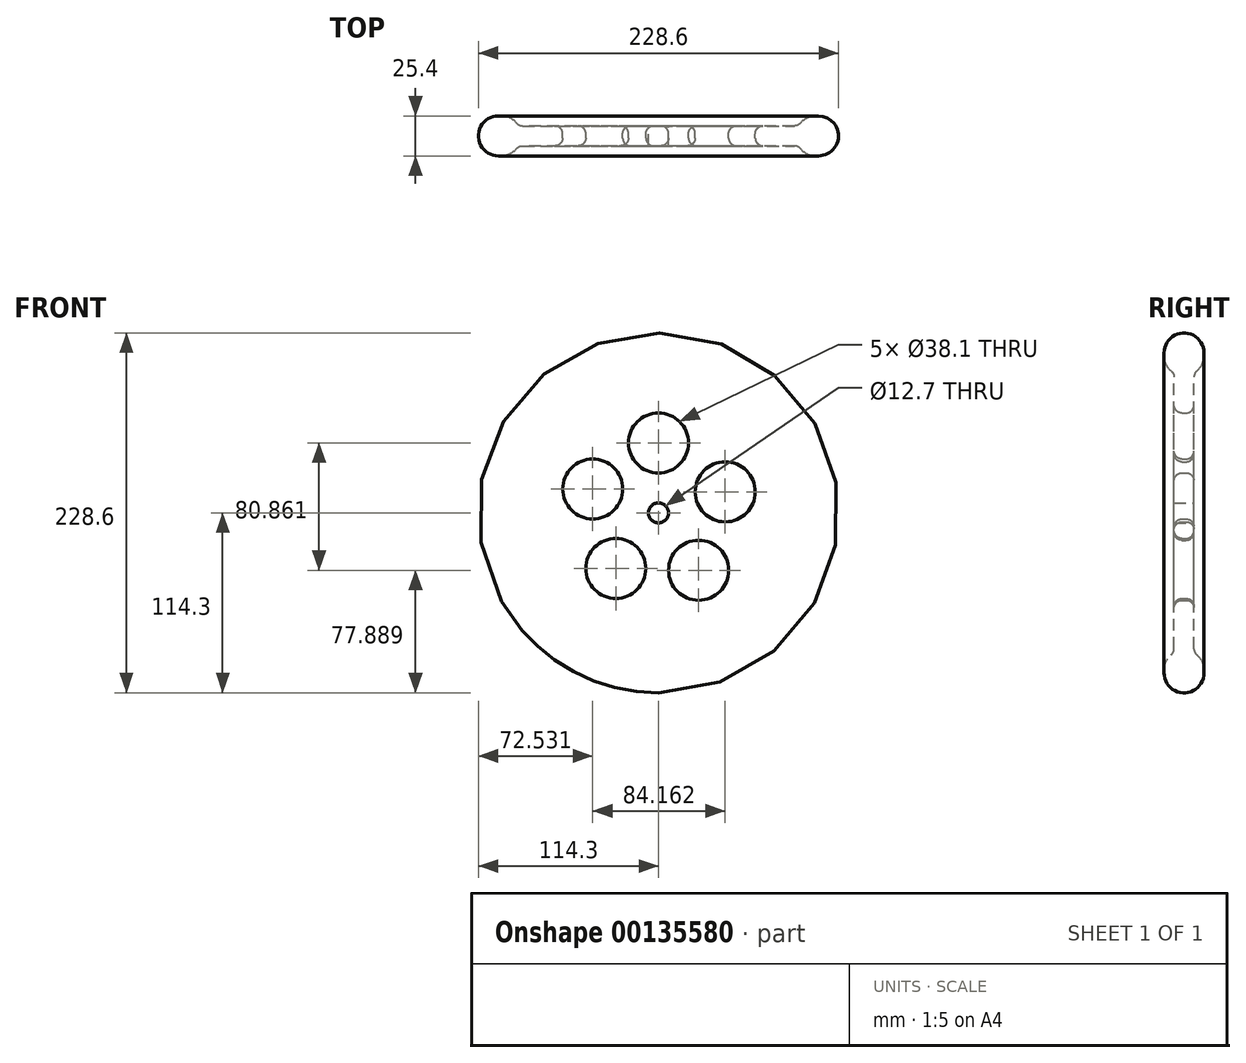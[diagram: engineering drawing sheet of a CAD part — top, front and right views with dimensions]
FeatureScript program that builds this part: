
annotation { "Feature Type Name" : "Feature", "Feature Type Description" : "" }
export const myFeature = defineFeature(function(context is Context, id is Id, definition is map)
    precondition{}
    {
        {
            var Q0;
            Q0=qCreatedBy(makeId("Front.planeOp"),FACE);
            var sketch = newSketch(context, id + "F0", { "sketchPlane" : qUnion([Q0])});
            skCircle(sketch, "E0", {"center": v(0, 0) * mm, "radius": 114.3 * mm});
            skCircle(sketch, "E1", {"center": v(0, 0) * mm, "radius": 88.9 * mm});
            skLineSegment(sketch, "E2", {"start": v(0, 0) * mm, "end": v(0, 88.9) * mm, "construction": true});
            skCircle(sketch, "E3", {"center": v(0, 44.45) * mm, "radius": 19.05 * mm});
            skCircle(sketch, "E4.1.0", {"center": v(42.4, 13.37) * mm, "radius": 19.05 * mm});
            skCircle(sketch, "E4.2.0", {"center": v(25.5, -36.41) * mm, "radius": 19.05 * mm});
            skCircle(sketch, "E4.3.0", {"center": v(-27.06, -35.26) * mm, "radius": 19.05 * mm});
            skCircle(sketch, "E4.4.0", {"center": v(-41.77, 15.2) * mm, "radius": 19.05 * mm});
            skLineSegment(sketch, "E4.anchor1", {"start": v(0, 0) * mm, "end": v(0, 44.45) * mm, "construction": true});
            skLineSegment(sketch, "E4.anchor2", {"start": v(0, 0) * mm, "end": v(-41.77, 15.2) * mm, "construction": true});
            skCircle(sketch, "E5", {"center": v(0, 0) * mm, "radius": 6.35 * mm});
            skSolve(sketch);
        }
        {
            var Q0;
            Q0 = qSketchRegion(id + "F0", true);
            extrude(context, id + "F1", {"entities" : qUnion([Q0]), "endBound" : BoundingType.SYMMETRIC, "depth" : 25.4 * mm});
        }
        {
            var Q0;
            Q0=makeQuery(id+"F0.imprint","IMPRINT",FACE,{"disambiguationData":[TD([[makeQuery(id+"F0.imprint","IMPRINT",EDGE,{"derivedFrom":sQuery(id+"F0.wireOp",EDGE,"E1")}),1.0]])]});
            extrude(context, id + "F2", {"entities" : qUnion([Q0]), "operationType" : NewBodyOperationType.ADD, "endBound" : BoundingType.SYMMETRIC, "depth" : 12.7 * mm});
        }
        {
            var Q0;
            Q0=makeQuery(id+"F1.opExtrude","CAP_EDGE",EDGE,{"disambiguationData":[OSD([sQuery(id+"F0.wireOp",EDGE,"E0")])],"isStart":false});
            var Q1;
            Q1=makeQuery(id+"F1.opExtrude","CAP_EDGE",EDGE,{"disambiguationData":[OSD([sQuery(id+"F0.wireOp",EDGE,"E0")])],"isStart":true});
            var Q2;
            Q2=makeQuery(id+"F1.opExtrude","CAP_EDGE",EDGE,{"disambiguationData":[OSD([sQuery(id+"F0.wireOp",EDGE,"E1")])],"isStart":true});
            var Q3;
            Q3=makeQuery(id+"F1.opExtrude","CAP_EDGE",EDGE,{"disambiguationData":[OSD([sQuery(id+"F0.wireOp",EDGE,"E1")])],"isStart":false});
            fillet(context, id + "F3", {"entities" : qUnion([Q0, Q1, Q2, Q3]), "radius" : 12.7 * mm, "tangentPropagation" : true, "allowEdgeOverflow" : false});
        }
        {
            var Q0;
            Q0=makeQuery(id+"F2.opExtrude","CAP_EDGE",EDGE,{"disambiguationData":[OSD([sQuery(id+"F0.wireOp",EDGE,"E4.2.0")])],"isStart":false});
            var Q1;
            Q1=makeQuery(id+"F2.opExtrude","CAP_EDGE",EDGE,{"disambiguationData":[OSD([sQuery(id+"F0.wireOp",EDGE,"E4.2.0")])],"isStart":true});
            var Q2;
            Q2=makeQuery(id+"F2.opExtrude","CAP_EDGE",EDGE,{"disambiguationData":[OSD([sQuery(id+"F0.wireOp",EDGE,"E4.3.0")])],"isStart":false});
            var Q3;
            Q3=makeQuery(id+"F2.opExtrude","CAP_EDGE",EDGE,{"disambiguationData":[OSD([sQuery(id+"F0.wireOp",EDGE,"E4.3.0")])],"isStart":true});
            var Q4;
            Q4=makeQuery(id+"F2.opExtrude","CAP_EDGE",EDGE,{"disambiguationData":[OSD([sQuery(id+"F0.wireOp",EDGE,"E4.4.0")])],"isStart":false});
            var Q5;
            Q5=makeQuery(id+"F2.opExtrude","CAP_EDGE",EDGE,{"disambiguationData":[OSD([sQuery(id+"F0.wireOp",EDGE,"E4.4.0")])],"isStart":true});
            var Q6;
            Q6=makeQuery(id+"F2.opExtrude","CAP_EDGE",EDGE,{"disambiguationData":[OSD([sQuery(id+"F0.wireOp",EDGE,"E3")])],"isStart":false});
            var Q7;
            Q7=makeQuery(id+"F2.opExtrude","CAP_EDGE",EDGE,{"disambiguationData":[OSD([sQuery(id+"F0.wireOp",EDGE,"E3")])],"isStart":true});
            var Q8;
            Q8=makeQuery(id+"F2.opExtrude","CAP_EDGE",EDGE,{"disambiguationData":[OSD([sQuery(id+"F0.wireOp",EDGE,"E4.1.0")])],"isStart":true});
            var Q9;
            Q9=makeQuery(id+"F2.opExtrude","CAP_EDGE",EDGE,{"disambiguationData":[OSD([sQuery(id+"F0.wireOp",EDGE,"E4.1.0")])],"isStart":false});
            fillet(context, id + "F4", {"entities" : qUnion([Q0, Q1, Q2, Q3, Q4, Q5, Q6, Q7, Q8, Q9]), "radius" : 5.08 * mm, "tangentPropagation" : true, "allowEdgeOverflow" : false});
        }
        {
            var Q0;
            {var subQ0=sQuery(id+"F0.wireOp",EDGE,"E1");Q0=makeQuery(id+"F3.opFillet","BLEND_EDGE",EDGE,{"blendedFrom":[makeQuery(id+"F1.opExtrude","CAP_EDGE",EDGE,{"disambiguationData":[OSD([subQ0])],"isStart":false}),makeQuery(id+"F2.opExtrude","CAP_FACE",FACE,{"disambiguationData":[OSD([subQ0,sQuery(id+"F0.wireOp",EDGE,"E3"),sQuery(id+"F0.wireOp",EDGE,"E4.1.0"),sQuery(id+"F0.wireOp",EDGE,"E4.2.0"),sQuery(id+"F0.wireOp",EDGE,"E4.3.0"),sQuery(id+"F0.wireOp",EDGE,"E4.4.0")])],"isStart":false})],"blendedInto":[makeQuery(id+"F2.opExtrude","CAP_FACE",FACE,{"disambiguationData":[OSD([subQ0,sQuery(id+"F0.wireOp",EDGE,"E3"),sQuery(id+"F0.wireOp",EDGE,"E4.1.0"),sQuery(id+"F0.wireOp",EDGE,"E4.2.0"),sQuery(id+"F0.wireOp",EDGE,"E4.3.0"),sQuery(id+"F0.wireOp",EDGE,"E4.4.0")])],"isStart":false})]});}
            var Q1;
            {var subQ0=sQuery(id+"F0.wireOp",EDGE,"E1");Q1=makeQuery(id+"F3.opFillet","BLEND_EDGE",EDGE,{"blendedFrom":[makeQuery(id+"F1.opExtrude","CAP_EDGE",EDGE,{"disambiguationData":[OSD([subQ0])],"isStart":true}),makeQuery(id+"F2.opExtrude","CAP_FACE",FACE,{"disambiguationData":[OSD([subQ0,sQuery(id+"F0.wireOp",EDGE,"E3"),sQuery(id+"F0.wireOp",EDGE,"E4.1.0"),sQuery(id+"F0.wireOp",EDGE,"E4.2.0"),sQuery(id+"F0.wireOp",EDGE,"E4.3.0"),sQuery(id+"F0.wireOp",EDGE,"E4.4.0")])],"isStart":true})],"blendedInto":[makeQuery(id+"F2.opExtrude","CAP_FACE",FACE,{"disambiguationData":[OSD([subQ0,sQuery(id+"F0.wireOp",EDGE,"E3"),sQuery(id+"F0.wireOp",EDGE,"E4.1.0"),sQuery(id+"F0.wireOp",EDGE,"E4.2.0"),sQuery(id+"F0.wireOp",EDGE,"E4.3.0"),sQuery(id+"F0.wireOp",EDGE,"E4.4.0")])],"isStart":true})]});}
            fillet(context, id + "F5", {"entities" : qUnion([Q0, Q1]), "radius" : 5.08 * mm, "tangentPropagation" : true, "allowEdgeOverflow" : false});
        }
    });
